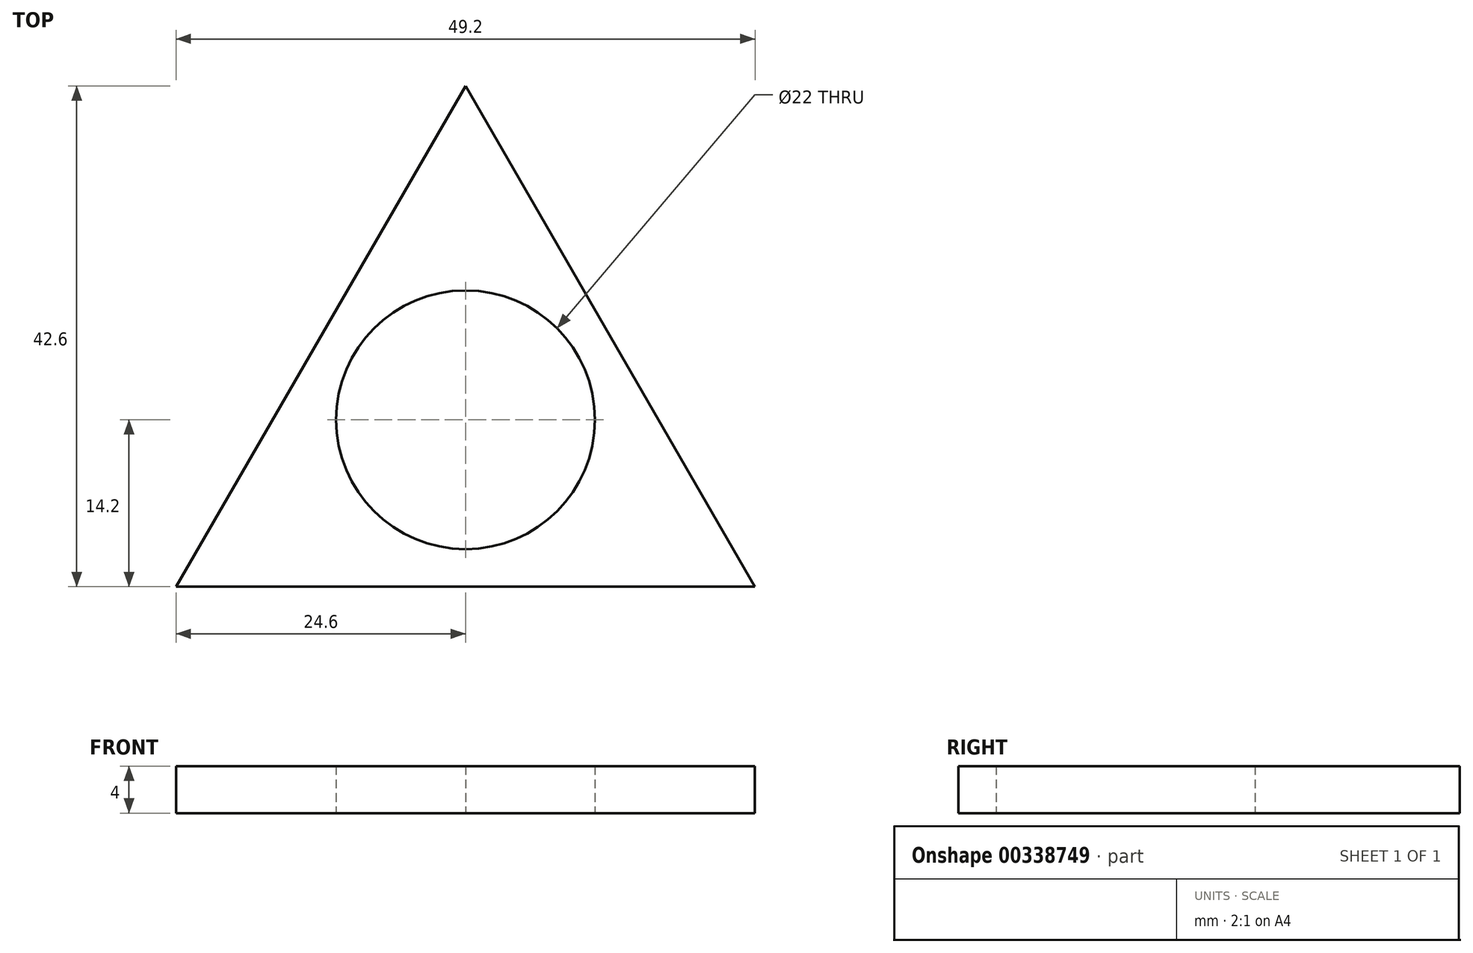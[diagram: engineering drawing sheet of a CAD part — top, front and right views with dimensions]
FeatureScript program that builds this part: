
annotation { "Feature Type Name" : "Feature", "Feature Type Description" : "" }
export const myFeature = defineFeature(function(context is Context, id is Id, definition is map)
    precondition{}
    {
        {
            var Q0;
            Q0=qCreatedBy(makeId("Top.planeOp"),FACE);
            var sketch = newSketch(context, id + "F0", { "sketchPlane" : qUnion([Q0])});
            skLineSegment(sketch, "E0.bottom", {"start": v(25, -4.2) * mm, "end": v(-25, -4.2) * mm, "construction": true});
            skLineSegment(sketch, "E0.top", {"start": v(25, 4.2) * mm, "end": v(-25, 4.2) * mm, "construction": true});
            skLineSegment(sketch, "E0.left", {"start": v(25, -4.2) * mm, "end": v(25, 4.2) * mm, "construction": true});
            skLineSegment(sketch, "E0.right", {"start": v(-25, -4.2) * mm, "end": v(-25, 4.2) * mm, "construction": true});
            skPoint(sketch, "E0.middle", {"position": v(0, 0) * mm});
            skCircle(sketch, "E1", {"center": v(0, 0) * mm, "radius": 11 * mm});
            skCircle(sketch, "E2.cCircle", {"center": v(0, 0) * mm, "radius": 14.2 * mm, "construction": true});
            skLineSegment(sketch, "E2.0", {"start": v(24.6, -14.2) * mm, "end": v(-24.6, -14.2) * mm});
            skLineSegment(sketch, "E2.1", {"start": v(-24.6, -14.2) * mm, "end": v(0, 28.4) * mm});
            skLineSegment(sketch, "E2.2", {"start": v(0, 28.4) * mm, "end": v(24.6, -14.2) * mm});
            skPoint(sketch, "E2.0.midPoint", {"position": v(0, -14.2) * mm});
            skSolve(sketch);
        }
        {
            var Q0;
            Q0=makeQuery(id+"F0.imprint","IMPRINT",FACE,{"disambiguationData":[TD([[makeQuery(id+"F0.imprint","IMPRINT",EDGE,{"derivedFrom":sQuery(id+"F0.wireOp",EDGE,"E1")}),-1.0]])]});
            extrude(context, id + "F1", {"entities" : qUnion([Q0]), "depth" : 4 * mm});
        }
    });
